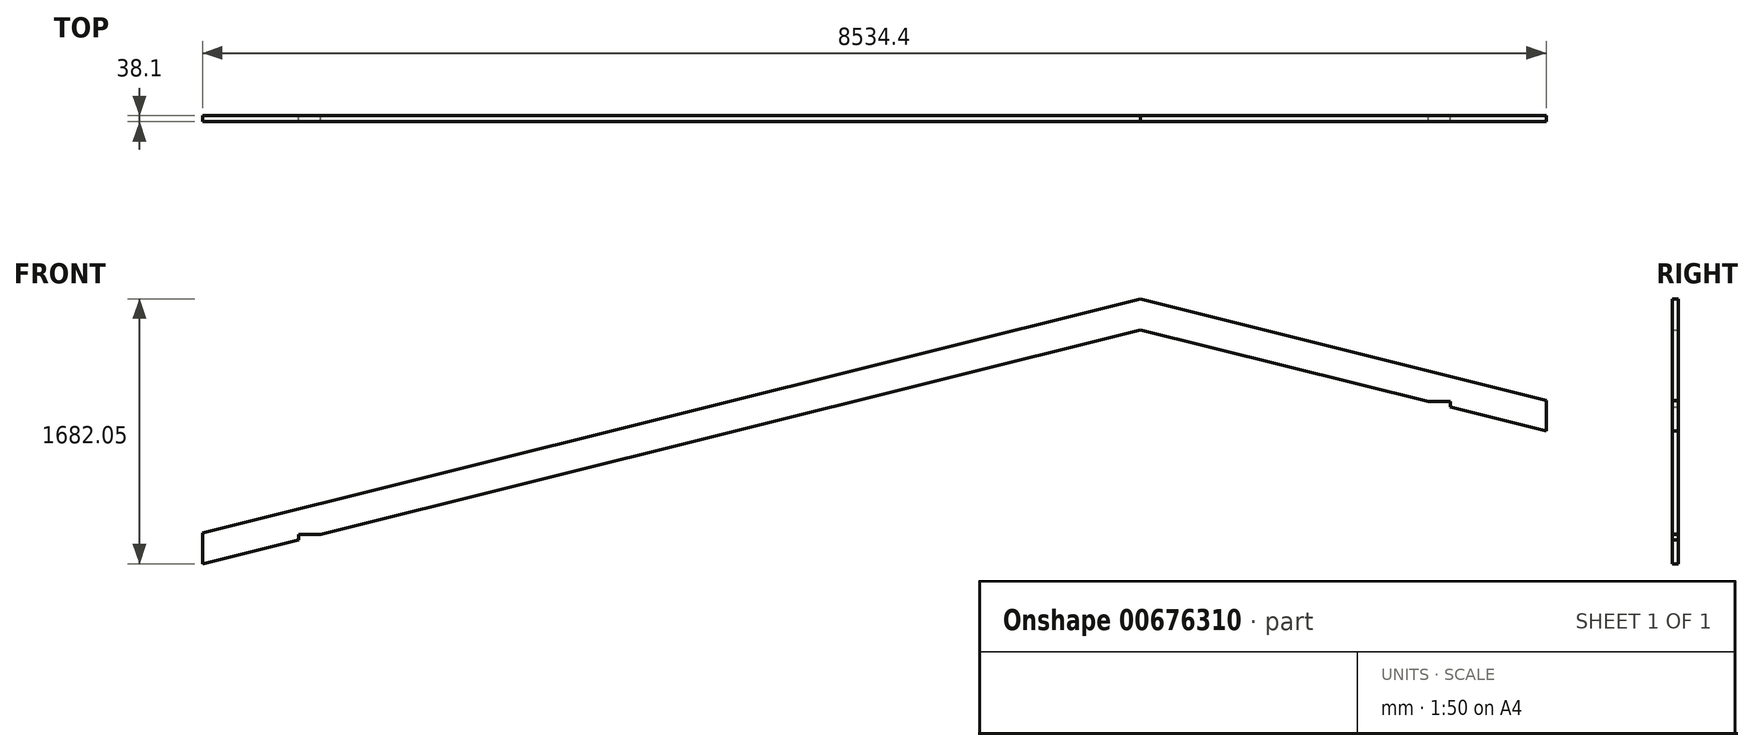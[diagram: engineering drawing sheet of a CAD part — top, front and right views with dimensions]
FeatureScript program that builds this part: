
annotation { "Feature Type Name" : "Feature", "Feature Type Description" : "" }
export const myFeature = defineFeature(function(context is Context, id is Id, definition is map)
    precondition{}
    {
        {
            var Q0;
            Q0=qCreatedBy(makeId("Front.planeOp"),FACE);
            var sketch = newSketch(context, id + "F0", { "sketchPlane" : qUnion([Q0])});
            skLineSegment(sketch, "E0", {"start": v(-5958.76, -1289.32) * mm, "end": v(0, 196.36) * mm});
            skLineSegment(sketch, "E1", {"start": v(0, 196.36) * mm, "end": v(2575.64, -447.55) * mm});
            skLineSegment(sketch, "E2", {"start": v(2575.64, -447.55) * mm, "end": v(2575.64, -643.9) * mm});
            skLineSegment(sketch, "E3", {"start": v(2575.64, -643.9) * mm, "end": v(1966.04, -491.5) * mm});
            skLineSegment(sketch, "E4", {"start": v(0, 0) * mm, "end": v(-5209.46, -1298.86) * mm});
            skLineSegment(sketch, "E5", {"start": v(-5958.76, -1485.69) * mm, "end": v(-5958.76, -1289.32) * mm});
            skLineSegment(sketch, "E6", {"start": v(0, 196.36) * mm, "end": v(0, 0) * mm, "construction": true});
            skLineSegment(sketch, "E7", {"start": v(0, 0) * mm, "end": v(46.2, 184.81) * mm, "construction": true});
            skLineSegment(sketch, "E8.trimOffspring", {"start": v(-5349.16, -1333.7) * mm, "end": v(-5958.76, -1485.69) * mm});
            skLineSegment(sketch, "E9.trimOffspring", {"start": v(1826.34, -456.58) * mm, "end": v(0, 0) * mm});
            skLineSegment(sketch, "E10", {"start": v(1966.04, -491.5) * mm, "end": v(1966.04, -456.58) * mm});
            skLineSegment(sketch, "E11", {"start": v(1966.04, -456.58) * mm, "end": v(1826.34, -456.58) * mm});
            skLineSegment(sketch, "E12", {"start": v(-5349.16, -1333.7) * mm, "end": v(-5349.16, -1298.86) * mm});
            skLineSegment(sketch, "E13", {"start": v(-5349.16, -1298.86) * mm, "end": v(-5209.46, -1298.86) * mm});
            skLineSegment(sketch, "E14.bottom", {"start": v(-5349.16, -1298.86) * mm, "end": v(-1831.26, -1298.86) * mm, "construction": true});
            skLineSegment(sketch, "E14.top", {"start": v(-5349.16, -4042.06) * mm, "end": v(-1831.26, -4042.06) * mm, "construction": true});
            skLineSegment(sketch, "E14.left", {"start": v(-5349.16, -1298.86) * mm, "end": v(-5349.16, -4042.06) * mm, "construction": true});
            skLineSegment(sketch, "E14.right", {"start": v(-1831.26, -1298.86) * mm, "end": v(-1831.26, -4042.06) * mm, "construction": true});
            skLineSegment(sketch, "E15.bottom", {"start": v(1966.04, -456.58) * mm, "end": v(-1831.26, -456.58) * mm, "construction": true});
            skLineSegment(sketch, "E15.top", {"start": v(1966.04, -4042.06) * mm, "end": v(-1831.26, -4042.06) * mm, "construction": true});
            skLineSegment(sketch, "E15.left", {"start": v(1966.04, -456.58) * mm, "end": v(1966.04, -4042.06) * mm, "construction": true});
            skLineSegment(sketch, "E15.right", {"start": v(-1831.26, -456.58) * mm, "end": v(-1831.26, -4042.06) * mm, "construction": true});
            skSolve(sketch);
        }
        {
            var Q0;
            Q0 = qSketchRegion(id + "F0", true);
            extrude(context, id + "F1", {"entities" : qUnion([Q0]), "depth" : 38.1 * mm, "offsetDistance" : 25.4 * mm});
        }
    });
